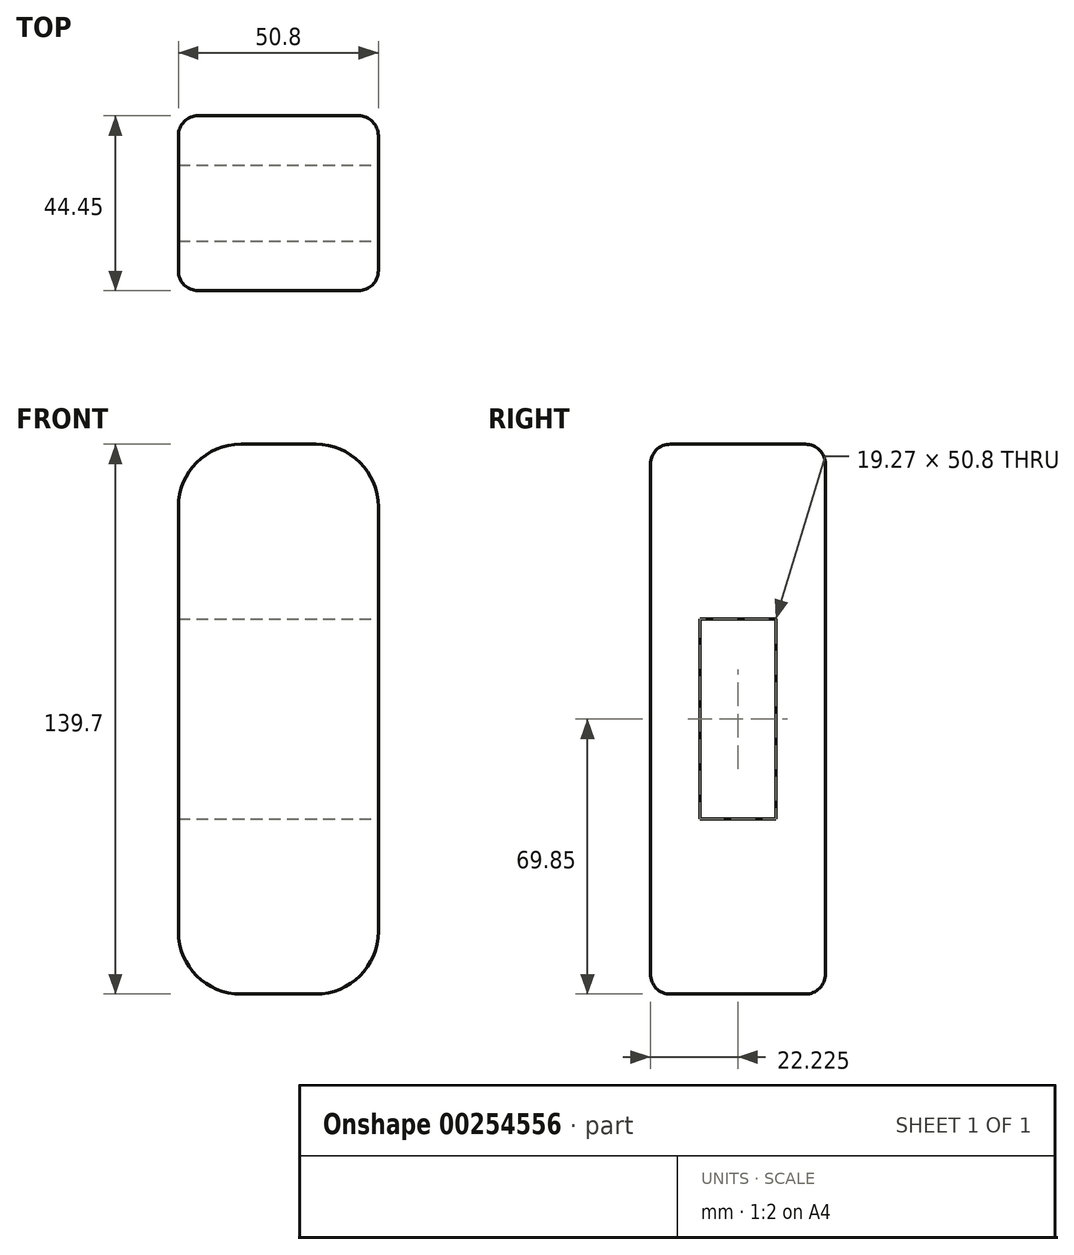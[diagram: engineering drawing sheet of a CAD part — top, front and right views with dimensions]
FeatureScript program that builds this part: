
annotation { "Feature Type Name" : "Feature", "Feature Type Description" : "" }
export const myFeature = defineFeature(function(context is Context, id is Id, definition is map)
    precondition{}
    {
        {
            var Q0;
            Q0=qCreatedBy(makeId("Front.planeOp"),FACE);
            var sketch = newSketch(context, id + "F0", { "sketchPlane" : qUnion([Q0])});
            skLineSegment(sketch, "E0.bottom", {"start": v(-9.52, -69.85) * mm, "end": v(9.53, -69.85) * mm});
            skLineSegment(sketch, "E0.top", {"start": v(-9.53, 69.85) * mm, "end": v(9.53, 69.85) * mm});
            skLineSegment(sketch, "E0.left", {"start": v(-25.4, -53.98) * mm, "end": v(-25.4, 53.98) * mm});
            skLineSegment(sketch, "E0.right", {"start": v(25.4, -53.98) * mm, "end": v(25.4, 53.98) * mm});
            skPoint(sketch, "E0.middle", {"position": v(0, 0) * mm});
            skPoint(sketch, "E1.visualSharp", {"position": v(-25.4, 69.85) * mm});
            skArc(sketch, "E1.filletArc", {"start": v(-9.53, 69.85) * mm, "mid": v(-20.75, 65.2) * mm, "end": v(-25.4, 53.98) * mm});
            skPoint(sketch, "E2.visualSharp", {"position": v(25.4, 69.85) * mm});
            skArc(sketch, "E2.filletArc", {"start": v(25.4, 53.98) * mm, "mid": v(20.75, 65.2) * mm, "end": v(9.53, 69.85) * mm});
            skPoint(sketch, "E3.visualSharp", {"position": v(25.4, -69.85) * mm});
            skArc(sketch, "E3.filletArc", {"start": v(9.53, -69.85) * mm, "mid": v(20.75, -65.2) * mm, "end": v(25.4, -53.98) * mm});
            skPoint(sketch, "E4.visualSharp", {"position": v(-25.4, -69.85) * mm});
            skArc(sketch, "E4.filletArc", {"start": v(-25.4, -53.98) * mm, "mid": v(-20.75, -65.2) * mm, "end": v(-9.52, -69.85) * mm});
            skSolve(sketch);
        }
        {
            var Q0;
            Q0 = qSketchRegion(id + "F0", true);
            extrude(context, id + "F1", {"entities" : qUnion([Q0]), "depth" : 44.45 * mm});
        }
        {
            var Q0;
            Q0=makeQuery(id+"F1.opExtrude","CAP_EDGE",EDGE,{"disambiguationData":[OSD([sQuery(id+"F0.wireOp",EDGE,"E0.top")])],"isStart":false});
            var Q1;
            Q1=makeQuery(id+"F1.opExtrude","CAP_FACE",FACE,{"disambiguationData":[OSD([sQuery(id+"F0.wireOp",EDGE,"E0.bottom"),sQuery(id+"F0.wireOp",EDGE,"E0.top"),sQuery(id+"F0.wireOp",EDGE,"E0.left"),sQuery(id+"F0.wireOp",EDGE,"E0.right"),sQuery(id+"F0.wireOp",EDGE,"E1.filletArc"),sQuery(id+"F0.wireOp",EDGE,"E2.filletArc"),sQuery(id+"F0.wireOp",EDGE,"E3.filletArc"),sQuery(id+"F0.wireOp",EDGE,"E4.filletArc")])],"isStart":false});
            var Q2;
            Q2=makeQuery(id+"F1.opExtrude","CAP_EDGE",EDGE,{"disambiguationData":[OSD([sQuery(id+"F0.wireOp",EDGE,"E0.top")])],"isStart":true});
            var Q3;
            Q3=makeQuery(id+"F1.opExtrude","CAP_EDGE",EDGE,{"disambiguationData":[OSD([sQuery(id+"F0.wireOp",EDGE,"E0.right")])],"isStart":true});
            fillet(context, id + "F2", {"entities" : qUnion([Q0, Q1, Q2, Q3]), "radius" : 5.08 * mm, "tangentPropagation" : true, "allowEdgeOverflow" : false});
        }
        {
            var Q0;
            Q0=makeQuery(id+"F1.opExtrude","SWEPT_FACE",FACE,{"disambiguationData":[OSD([sQuery(id+"F0.wireOp",EDGE,"E0.right")])]});
            var sketch = newSketch(context, id + "F3", { "sketchPlane" : qUnion([Q0])});
            skLineSegment(sketch, "E5.bottom", {"start": v(-12.6, 25.4) * mm, "end": v(-31.86, 25.4) * mm});
            skLineSegment(sketch, "E5.top", {"start": v(-12.6, -25.4) * mm, "end": v(-31.86, -25.4) * mm});
            skLineSegment(sketch, "E5.left", {"start": v(-12.6, 25.4) * mm, "end": v(-12.6, -25.4) * mm});
            skLineSegment(sketch, "E5.right", {"start": v(-31.86, 25.4) * mm, "end": v(-31.86, -25.4) * mm});
            skPoint(sketch, "E5.middle", {"position": v(-22.23, 0) * mm});
            skSolve(sketch);
        }
        {
            var Q0;
            Q0 = qSketchRegion(id + "F3", true);
            extrude(context, id + "F4", {"entities" : qUnion([Q0]), "operationType" : NewBodyOperationType.REMOVE, "endBound" : BoundingType.THROUGH_ALL, "oppositeDirection" : true, "depth" : 25.4 * mm});
        }
    });
